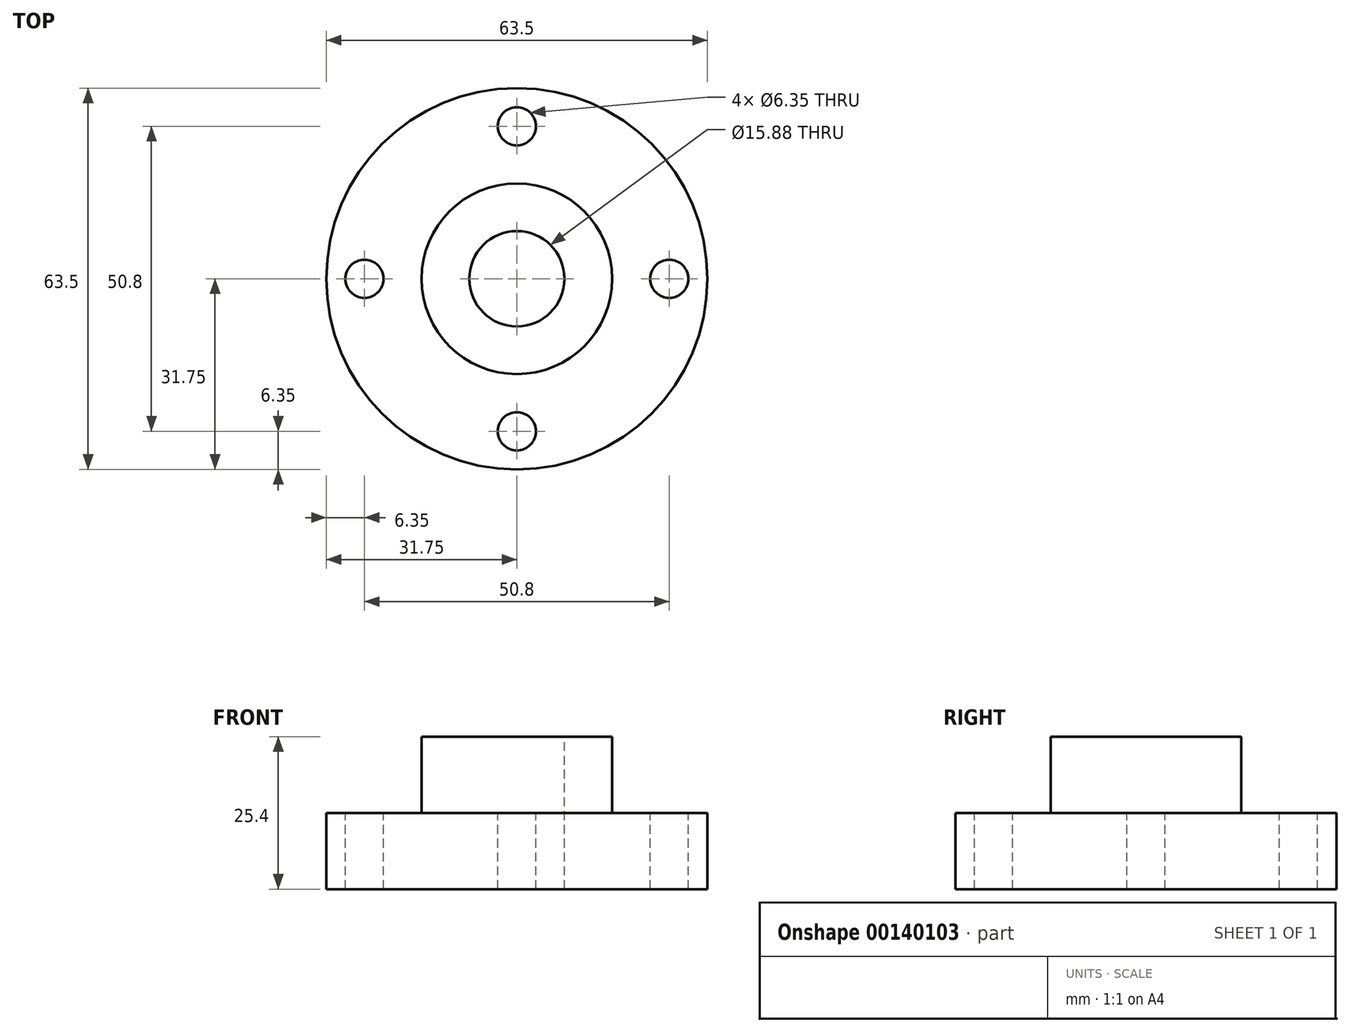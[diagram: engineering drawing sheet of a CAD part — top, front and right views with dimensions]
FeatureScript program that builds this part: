
annotation { "Feature Type Name" : "Feature", "Feature Type Description" : "" }
export const myFeature = defineFeature(function(context is Context, id is Id, definition is map)
    precondition{}
    {
        {
            var Q0;
            Q0=qCreatedBy(makeId("Front.planeOp"),FACE);
            var sketch = newSketch(context, id + "F0", { "sketchPlane" : qUnion([Q0])});
            skLineSegment(sketch, "E0", {"start": v(0, 43.09) * mm, "end": v(0, -38.84) * mm, "construction": true});
            skLineSegment(sketch, "E1.bottom", {"start": v(0, 0) * mm, "end": v(-31.75, 0) * mm});
            skLineSegment(sketch, "E1.top", {"start": v(0, 12.7) * mm, "end": v(-31.75, 12.7) * mm});
            skLineSegment(sketch, "E1.left", {"start": v(0, 0) * mm, "end": v(0, 12.7) * mm});
            skLineSegment(sketch, "E1.right", {"start": v(-31.75, 0) * mm, "end": v(-31.75, 12.7) * mm});
            skPoint(sketch, "E2.oppositeSnap0", {"position": v(-15.88, 12.7) * mm});
            skLineSegment(sketch, "E2.bottom", {"start": v(0, 12.7) * mm, "end": v(-15.88, 12.7) * mm});
            skLineSegment(sketch, "E2.top", {"start": v(0, 25.4) * mm, "end": v(-15.88, 25.4) * mm});
            skLineSegment(sketch, "E2.left", {"start": v(0, 12.7) * mm, "end": v(0, 25.4) * mm});
            skLineSegment(sketch, "E2.right", {"start": v(-15.88, 12.7) * mm, "end": v(-15.88, 25.4) * mm});
            skSolve(sketch);
        }
        {
            var Q0;
            Q0 = qSketchRegion(id + "F0", true);
            var Q1;
            Q1=sQuery(id+"F0.wireOp",EDGE,"E0");
            revolve(context, id + "F1", {"entities" : qUnion([Q0]), "axis" : qUnion([Q1]), "revolveType" : RevolveType.FULL});
        }
        {
            var Q0;
            Q0=makeQuery(id+"F1.opRevolve","SWEPT_FACE",FACE,{"disambiguationData":[OSD([sQuery(id+"F0.wireOp",EDGE,"E2.top")])]});
            var sketch = newSketch(context, id + "F2", { "sketchPlane" : qUnion([Q0])});
            skCircle(sketch, "E3", {"center": v(0, 0) * mm, "radius": 7.94 * mm});
            skSolve(sketch);
        }
        {
            var Q0;
            Q0 = qSketchRegion(id + "F2", true);
            extrude(context, id + "F3", {"entities" : qUnion([Q0]), "operationType" : NewBodyOperationType.REMOVE, "endBound" : BoundingType.THROUGH_ALL, "oppositeDirection" : true, "depth" : 25.4 * mm});
        }
        {
            var Q0;
            Q0=makeQuery(id+"F1.opRevolve","SWEPT_FACE",FACE,{"disambiguationData":[OSD([sQuery(id+"F0.wireOp",EDGE,"E1.top")])]});
            var sketch = newSketch(context, id + "F4", { "sketchPlane" : qUnion([Q0])});
            skLineSegment(sketch, "E4", {"start": v(0, 31.75) * mm, "end": v(0, -31.75) * mm, "construction": true});
            skLineSegment(sketch, "E5", {"start": v(-31.75, 0) * mm, "end": v(31.75, 0) * mm, "construction": true});
            skCircle(sketch, "E6", {"center": v(0, 0) * mm, "radius": 25.4 * mm, "construction": true});
            skCircle(sketch, "E7", {"center": v(0, 25.4) * mm, "radius": 3.18 * mm});
            skCircle(sketch, "E8", {"center": v(25.4, 0) * mm, "radius": 3.18 * mm});
            skCircle(sketch, "E9", {"center": v(0, -25.4) * mm, "radius": 3.18 * mm});
            skCircle(sketch, "E10", {"center": v(-25.4, 0) * mm, "radius": 3.18 * mm});
            skSolve(sketch);
        }
        {
            var Q0;
            Q0 = qSketchRegion(id + "F4", true);
            extrude(context, id + "F5", {"entities" : qUnion([Q0]), "operationType" : NewBodyOperationType.REMOVE, "endBound" : BoundingType.THROUGH_ALL, "oppositeDirection" : true, "depth" : 25.4 * mm});
        }
    });
